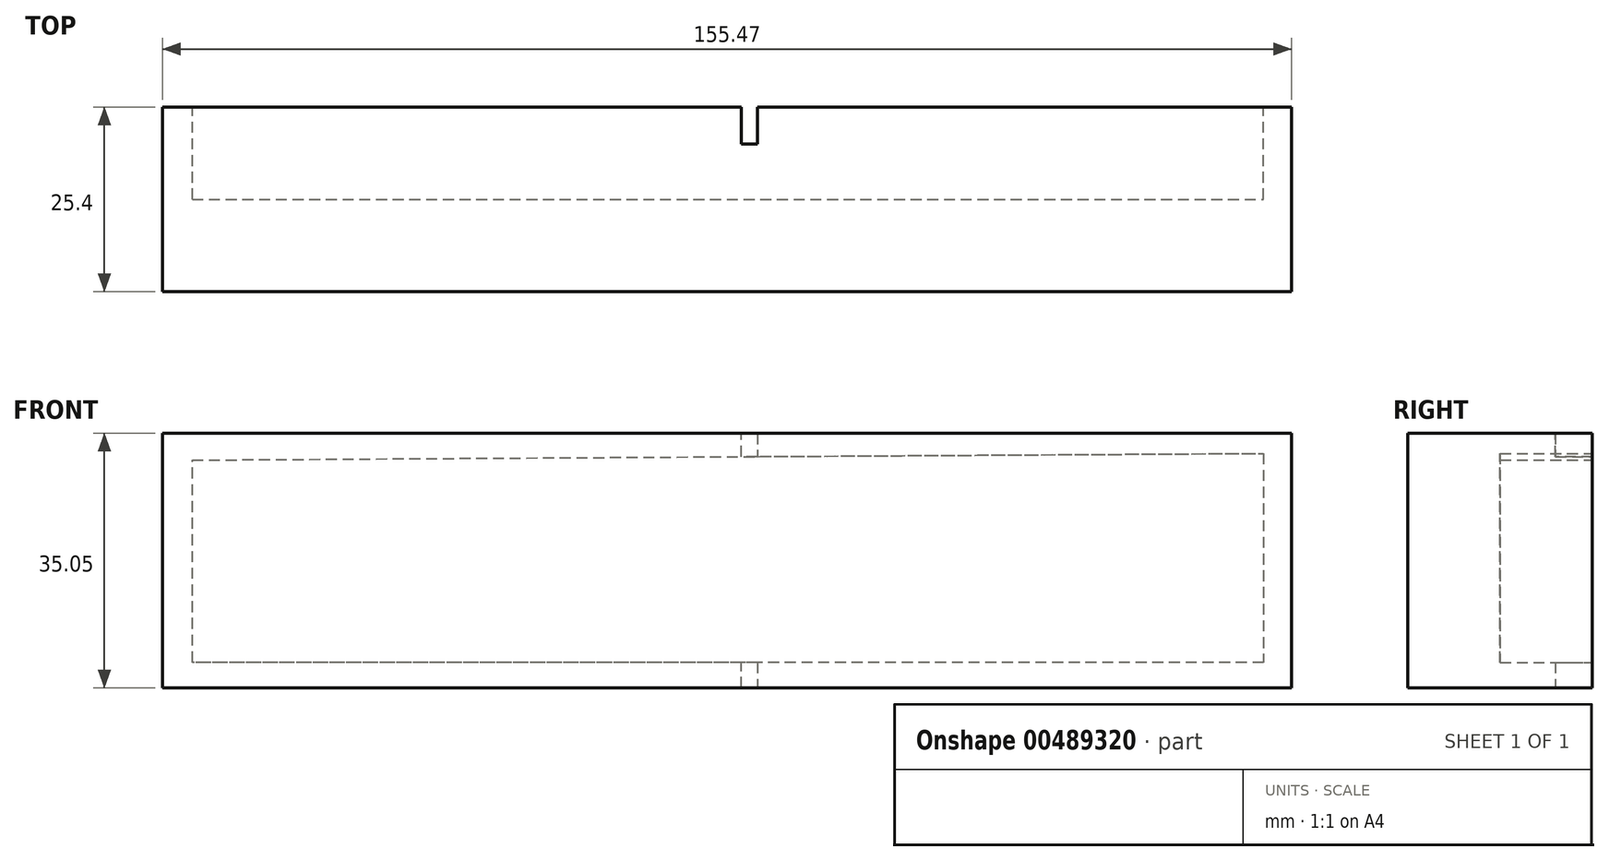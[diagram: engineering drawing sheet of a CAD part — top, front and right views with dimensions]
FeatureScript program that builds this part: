
annotation { "Feature Type Name" : "Feature", "Feature Type Description" : "" }
export const myFeature = defineFeature(function(context is Context, id is Id, definition is map)
    precondition{}
    {
        {
            var Q0;
            Q0=qCreatedBy(makeId("Front.planeOp"),FACE);
            var sketch = newSketch(context, id + "F0", { "sketchPlane" : qUnion([Q0])});
            skLineSegment(sketch, "E0", {"start": v(0, 0) * mm, "end": v(-61.66, 0) * mm});
            skLineSegment(sketch, "E1", {"start": v(-61.66, 0) * mm, "end": v(-61.66, -35.05) * mm});
            skLineSegment(sketch, "E2", {"start": v(0, 0) * mm, "end": v(93.8, 0) * mm});
            skLineSegment(sketch, "E3", {"start": v(93.8, 0) * mm, "end": v(93.8, -35.05) * mm});
            skLineSegment(sketch, "E4", {"start": v(-61.66, -35.05) * mm, "end": v(93.8, -35.05) * mm});
            skSolve(sketch);
        }
        {
            var Q0;
            Q0=makeQuery(id+"F0.imprint","IMPRINT",FACE,{"disambiguationData":[TD([[makeQuery(id+"F0.imprint","IMPRINT",EDGE,{"derivedFrom":sQuery(id+"F0.wireOp",EDGE,"E0")}),1.0]])]});
            extrude(context, id + "F1", {"entities" : qUnion([Q0]), "depth" : 25.4 * mm});
        }
        {
            var Q0;
            Q0=makeQuery(id+"F1.opExtrude","CAP_FACE",FACE,{"disambiguationData":[OSD([sQuery(id+"F0.wireOp",EDGE,"E0"),sQuery(id+"F0.wireOp",EDGE,"E1"),sQuery(id+"F0.wireOp",EDGE,"E2"),sQuery(id+"F0.wireOp",EDGE,"E3"),sQuery(id+"F0.wireOp",EDGE,"E4")])],"isStart":true});
            var sketch = newSketch(context, id + "F2", { "sketchPlane" : qUnion([Q0])});
            skLineSegment(sketch, "E5", {"start": v(-89.92, -2.77) * mm, "end": v(-89.92, -31.52) * mm});
            skLineSegment(sketch, "E6", {"start": v(-89.92, -31.52) * mm, "end": v(57.56, -31.52) * mm});
            skLineSegment(sketch, "E7", {"start": v(57.56, -31.52) * mm, "end": v(57.56, -3.69) * mm});
            skLineSegment(sketch, "E8", {"start": v(57.56, -3.69) * mm, "end": v(-89.92, -2.77) * mm});
            skSolve(sketch);
        }
        {
            var Q0;
            Q0=makeQuery(id+"F2.imprint","IMPRINT",FACE,{"disambiguationData":[TD([[makeQuery(id+"F2.imprint","IMPRINT",EDGE,{"derivedFrom":sQuery(id+"F2.wireOp",EDGE,"E5")}),1.0]])]});
            extrude(context, id + "F3", {"entities" : qUnion([Q0]), "operationType" : NewBodyOperationType.REMOVE, "oppositeDirection" : true, "depth" : 12.7 * mm});
        }
        {
            var Q0;
            Q0=makeQuery(id+"F1.opExtrude","CAP_FACE",FACE,{"disambiguationData":[OSD([sQuery(id+"F0.wireOp",EDGE,"E0"),sQuery(id+"F0.wireOp",EDGE,"E1"),sQuery(id+"F0.wireOp",EDGE,"E2"),sQuery(id+"F0.wireOp",EDGE,"E3"),sQuery(id+"F0.wireOp",EDGE,"E4")])],"isStart":true});
            var sketch = newSketch(context, id + "F4", { "sketchPlane" : qUnion([Q0])});
            skLineSegment(sketch, "E9", {"start": v(-20.23, -31.52) * mm, "end": v(-20.23, -35.05) * mm});
            skLineSegment(sketch, "E10", {"start": v(-20.23, -35.05) * mm, "end": v(-18.02, -35.05) * mm});
            skLineSegment(sketch, "E11", {"start": v(-18.02, -35.05) * mm, "end": v(-18.02, -31.52) * mm});
            skLineSegment(sketch, "E12", {"start": v(-18.02, -31.52) * mm, "end": v(-20.23, -31.52) * mm});
            skLineSegment(sketch, "E13", {"start": v(-20.23, 0) * mm, "end": v(-20.23, -3.2) * mm});
            skLineSegment(sketch, "E14", {"start": v(-20.23, -3.2) * mm, "end": v(-18.02, -3.23) * mm});
            skPoint(sketch, "E14.endSnap0", {"position": v(-16.18, -3.23) * mm});
            skLineSegment(sketch, "E15", {"start": v(-18.02, -3.23) * mm, "end": v(-18.02, 0) * mm});
            skLineSegment(sketch, "E16", {"start": v(-18.02, 0) * mm, "end": v(-20.23, 0) * mm});
            skSolve(sketch);
        }
        {
            var Q0;
            Q0 = qSketchRegion(id + "F4", true);
            extrude(context, id + "F5", {"entities" : qUnion([Q0]), "operationType" : NewBodyOperationType.REMOVE, "oppositeDirection" : true, "depth" : 5.08 * mm});
        }
    });
